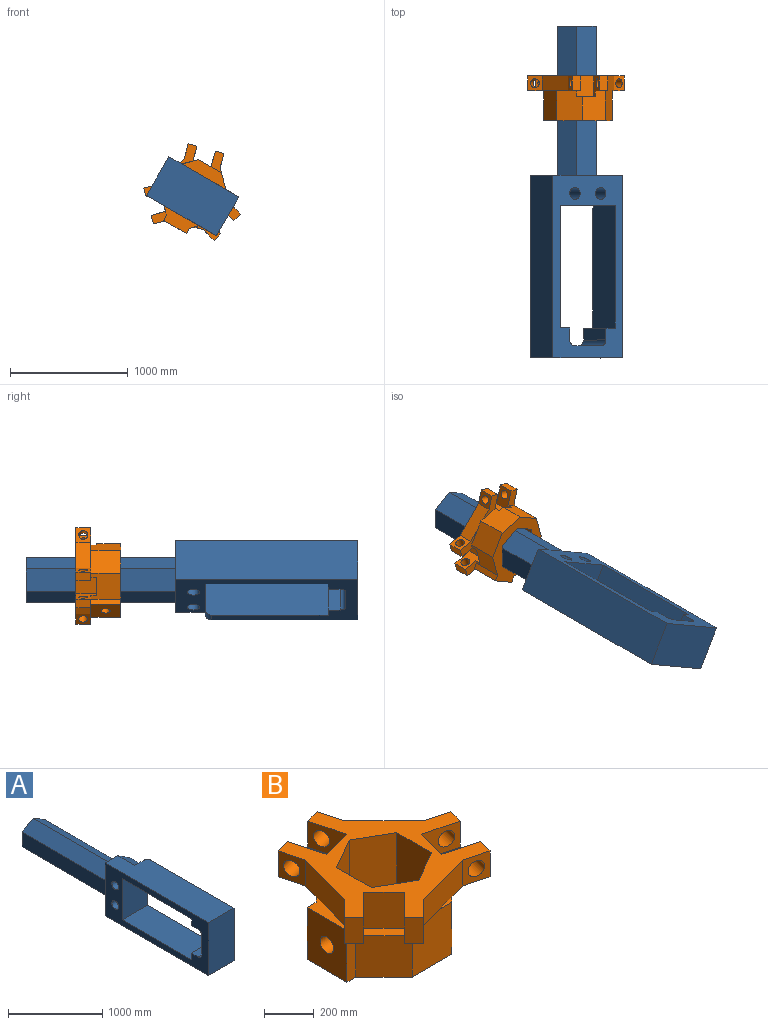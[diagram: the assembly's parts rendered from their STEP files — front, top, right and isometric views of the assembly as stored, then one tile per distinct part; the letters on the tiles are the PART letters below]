
ASSEMBLY  parts=2 mates=1
PART A: 30 faces, bbox 381x2819.4x685.8 mm
  f0: plane 1549.4x381mm, normal (0,0,1), area 541380.6mm2, adj f1,f3,f5,f18,f27,f28,f29
  f1: plane 1549.4x685.8mm, normal (1,0,0), area 401666.3mm2, adj f0,f3,f4,f5,f6,f7,f8,f9
  f2: plane 381x329.96mm, normal (0,1,0), area 89724.5mm2, adj f19,f20,f21,f22,f23,f24,f26
  f3: plane 685.8x381mm, normal (0,-1,0), area 261289.8mm2, adj f0,f1,f4,f18
  f4: plane 1549.4x381mm, normal (0,0,-1), area 590321.4mm2, adj f1,f3,f5,f18
  f5: plane 685.8x381mm, normal (0,1,0), area 154908.2mm2, adj f0,f1,f4,f18,f19,f20,f21,f22
  f6: plane 533.4x381mm, normal (0,-1,0), area 201289.9mm2, adj f1,f7,f16,f18,f27
  f7: plane 1041.4x381mm, normal (0,0,1), area 396773.4mm2, adj f1,f6,f8,f18
  f8: plane 381x88.9mm, normal (0,1,0), area 33870.9mm2, adj f1,f7,f9,f18
  f9: plane 381x101.6mm, normal (0,0,1), area 38709.6mm2, adj f1,f8,f10,f18
  f10: cylinder r=50.8mm len=381mm, axis (1,0,0), area 30402.4mm2, adj f1,f9,f11,f18
  f11: plane 381x254mm, normal (0,1,0), area 96774mm2, adj f1,f10,f12,f18
  f12: cylinder r=50.8mm len=381mm, axis (1,0,0), area 30402.4mm2, adj f1,f11,f13,f18
  f13: plane 381x101.6mm, normal (0,0,-1), area 38709.6mm2, adj f1,f12,f14,f18
  f14: plane 381x88.9mm, normal (0,1,0), area 33870.9mm2, adj f1,f13,f16,f18
  f15: cylinder r=50.8mm len=381mm, axis (1,0,0), area 121609.8mm2, adj f1,f18
  f16: plane 1041.4x381mm, normal (0,0,-1), area 396219.6mm2, adj f1,f6,f14,f18,f28,f29
  f17: cylinder r=50.8mm len=381mm, axis (1,0,0), area 121609.8mm2, adj f1,f18
  f18: plane 1549.4x685.8mm, normal (-1,0,0), area 437795.3mm2, adj f0,f3,f4,f5,f6,f7,f8,f9
  f19: plane 1270x164.98mm, normal (0.5,0,-0.87), area 241935mm2, adj f2,f5,f20,f24
  f20: plane 1270x190.5mm, normal (1,0,0), area 241935mm2, adj f2,f5,f19,f21
  f21: plane 1270x164.98mm, normal (0.5,0,0.87), area 241935mm2, adj f2,f5,f20,f22
  f22: plane 1270x164.98mm, normal (-0.5,0,0.87), area 241935mm2, adj f2,f5,f21,f23
  f23: plane 1270x190.5mm, normal (-1,0,0), area 241935mm2, adj f2,f5,f22,f24
  f24: plane 1270x164.98mm, normal (-0.5,0,-0.87), area 241935mm2, adj f2,f5,f19,f23
  f25: cone r=0mm half-angle=59deg, axis (0,1,0), area 5320.3mm2, adj f26
  f26: cylinder r=38.1mm len=635mm, axis (0,1,0), area 152012.2mm2, adj f2,f25
  f27: plane 254x190.5mm, normal (0.55,0,0.83), area 58153.9mm2, adj f0,f1,f5,f6,f28
  f28: plane 139.7x76.2mm, normal (0,1,0), area 6290.3mm2, adj f0,f16,f27,f29
  f29: cylinder r=50.8mm len=76.2mm, axis (0,0,1), area 6080.5mm2, adj f0,f1,f16,f28
PART B: 61 faces, bbox 819.4x819.4x381 mm
  f0: plane 177.8x156.26mm, normal (-0.26,0.97,0), area 28762.3mm2, adj f4,f6,f53,f56
  f1: plane 223.71x107.67mm, normal (0,0,-1), area 12727.5mm2, adj f15,f31,f48,f49,f50
  f2: plane 168.21x79.27mm, normal (0,0,1), area 9009mm2, adj f3,f15,f16,f45,f48
  f3: plane 177.8x156.26mm, normal (0.97,-0.26,0), area 28762.3mm2, adj f2,f4,f45,f48
  f4: plane 819.4x819.4mm, normal (0,0,1), area 189169.2mm2, adj f0,f3,f8,f9,f10,f11,f12,f17
  f5: plane 241.56x78.94mm, normal (0,0,1), area 9287.7mm2, adj f19,f24,f26,f32,f39
  f6: plane 168.21x79.27mm, normal (0,0,1), area 9009mm2, adj f0,f18,f19,f53,f56
  f7: plane 105.02x28.14mm, normal (0,0,1), area 1081.7mm2, adj f14,f15,f31
  f8: plane 381x170.48mm, normal (-0.5,0.87,0), area 74999.9mm2, adj f4,f9,f20,f21
  f9: plane 381x170.48mm, normal (0.5,0.87,0), area 74999.9mm2, adj f4,f8,f10,f21
  f10: plane 381x196.85mm, normal (1,0,0), area 56758.4mm2, adj f4,f9,f11,f21,f22
  f11: plane 381x170.48mm, normal (0.5,-0.87,0), area 74999.9mm2, adj f4,f10,f12,f21
  f12: plane 381x170.48mm, normal (-0.5,-0.87,0), area 74999.9mm2, adj f4,f11,f20,f21
  f13: plane 254x159.38mm, normal (-0.71,-0.71,0), area 49032.8mm2, adj f14,f21,f25,f29,f35,f37,f38,f41
  f14: plane 254x225.4mm, normal (0,-1,0), area 57250.6mm2, adj f7,f13,f15,f21,f29
  f15: plane 254x159.38mm, normal (0.71,-0.71,0), area 54760.8mm2, adj f1,f2,f7,f14,f16,f21,f48
  f16: plane 254x225.4mm, normal (1,0,0), area 50975.2mm2, adj f2,f15,f17,f21,f30,f45
  f17: plane 381x222.15mm, normal (0.71,0.71,0), area 97149.9mm2, adj f4,f16,f18,f21,f30,f33,f46,f57
  f18: plane 254x225.4mm, normal (0,1,0), area 50975.2mm2, adj f6,f17,f19,f21,f33,f56
  f19: plane 254x159.38mm, normal (-0.71,0.71,0), area 54760.8mm2, adj f5,f6,f18,f21,f24,f28,f53
  f20: plane 381x196.85mm, normal (-1,0,0), area 74999.8mm2, adj f4,f8,f12,f21
  f21: plane 594.95x544.15mm, normal (0,0,-1), area 156075.3mm2, adj f8,f9,f10,f11,f12,f13,f14,f15
  f22: cylinder r=76.2mm len=152.4mm, axis (1,0,0), area 36482.9mm2, adj f10,f23
  f23: plane 152.4x152.4mm, normal (1,0,0), area 13681.1mm2, adj f22,f27
  f24: plane 254x50.8mm, normal (0,1,0), area 12903.2mm2, adj f5,f19,f21,f26
  f25: plane 254x50.8mm, normal (0,-1,0), area 12903.2mm2, adj f13,f21,f26,f37
  f26: plane 254x225.4mm, normal (-1,0,0), area 52690.2mm2, adj f5,f21,f24,f25,f27,f37
  f27: cylinder r=38.1mm len=76.2mm, axis (1,0,0), area 18241.5mm2, adj f23,f26
  f28: plane 223.71x107.67mm, normal (0,0,-1), area 12727.5mm2, adj f19,f32,f53,f54,f55
  f29: plane 260.82x143.68mm, normal (0,0,-1), area 12008mm2, adj f13,f14,f31,f34,f35,f36
  f30: plane 154.06x137.86mm, normal (0,0,-1), area 11736mm2, adj f16,f17,f45,f46,f47
  f31: plane 303.46x127mm, normal (0.26,-0.97,0), area 39899.3mm2, adj f1,f4,f7,f29,f34,f49
  f32: plane 303.46x127mm, normal (-0.97,0.26,0), area 39899.3mm2, adj f4,f5,f28,f39,f54
  f33: plane 154.06x137.86mm, normal (0,0,-1), area 11736mm2, adj f17,f18,f56,f57,f58
  f34: plane 127x89.8mm, normal (0.71,-0.71,0), area 11568.6mm2, adj f4,f29,f31,f36,f44
  f35: plane 177.8x125.72mm, normal (-0.71,0.71,0), area 20600.9mm2, adj f4,f13,f29,f36,f41,f42,f44
  f36: plane 127x53.88mm, normal (-0.71,-0.71,0), area 9677.4mm2, adj f4,f29,f34,f35
  f37: plane 143.68x124.27mm, normal (0,0,-1), area 8764mm2, adj f13,f25,f26,f38,f39,f40
  f38: plane 177.8x125.72mm, normal (0.71,-0.71,0), area 20600.9mm2, adj f4,f13,f37,f40,f41,f42,f43
  f39: plane 127x89.8mm, normal (-0.71,0.71,0), area 11568.6mm2, adj f4,f5,f32,f37,f40,f43
  f40: plane 127x53.88mm, normal (-0.71,-0.71,0), area 9677.4mm2, adj f4,f37,f38,f39
  f41: plane 150.31x150.31mm, normal (0,0,1), area 8217.8mm2, adj f13,f35,f38,f42
  f42: plane 177.8x114.39mm, normal (-0.71,-0.71,0), area 28762.3mm2, adj f4,f35,f38,f41
  f43: cylinder r=38.1mm len=107.76mm, axis (0.71,-0.71,0), area 18241.5mm2, adj f38,f39
  f44: cylinder r=38.1mm len=107.76mm, axis (0.71,-0.71,0), area 18241.5mm2, adj f34,f35
  f45: plane 177.8x171.74mm, normal (-0.26,-0.97,0), area 19987.5mm2, adj f2,f3,f4,f16,f30,f47,f52
  f46: plane 127x122.67mm, normal (0.26,0.97,0), area 11568.6mm2, adj f4,f17,f30,f47,f52
  f47: plane 127x73.6mm, normal (0.97,-0.26,0), area 9677.4mm2, adj f4,f30,f45,f46
  f48: plane 177.8x171.74mm, normal (0.26,0.97,0), area 20366.8mm2, adj f1,f2,f3,f4,f15,f50,f51
  f49: plane 127x122.67mm, normal (-0.26,-0.97,0), area 11568.6mm2, adj f1,f4,f31,f50,f51
  f50: plane 127x73.6mm, normal (0.97,-0.26,0), area 9677.4mm2, adj f1,f4,f48,f49
  f51: cylinder r=38.1mm len=93.33mm, axis (0.26,0.97,0), area 18241.5mm2, adj f48,f49
  f52: cylinder r=38.1mm len=93.33mm, axis (0.26,0.97,0), area 18241.5mm2, adj f45,f46
  f53: plane 177.8x171.74mm, normal (0.97,0.26,0), area 20366.8mm2, adj f0,f4,f6,f19,f28,f55,f60
  f54: plane 127x122.67mm, normal (-0.97,-0.26,0), area 11568.6mm2, adj f4,f28,f32,f55,f60
  f55: plane 127x73.6mm, normal (-0.26,0.97,0), area 9677.4mm2, adj f4,f28,f53,f54
  f56: plane 177.8x171.74mm, normal (-0.97,-0.26,0), area 19987.5mm2, adj f0,f4,f6,f18,f33,f58,f59
  f57: plane 127x122.67mm, normal (0.97,0.26,0), area 11568.6mm2, adj f4,f17,f33,f58,f59
  f58: plane 127x73.6mm, normal (-0.26,0.97,0), area 9677.4mm2, adj f4,f33,f56,f57
  f59: cylinder r=38.1mm len=93.33mm, axis (0.97,0.26,0), area 18241.5mm2, adj f56,f57
  f60: cylinder r=38.1mm len=93.33mm, axis (0.97,0.26,0), area 18241.5mm2, adj f53,f54
PLACE A rot(axis=(0,1,0),120deg) t=(-758.03,1068.03,327.42)mm
PLACE B rot(axis=(-0.77,-0.45,-0.45),104.5deg) t=(-651.87,2042.36,511.29)mm
MATE slider B.f21 <-> A.f25  axis (0,-1,0) through (-662.78,1788.36,492.39)mm
